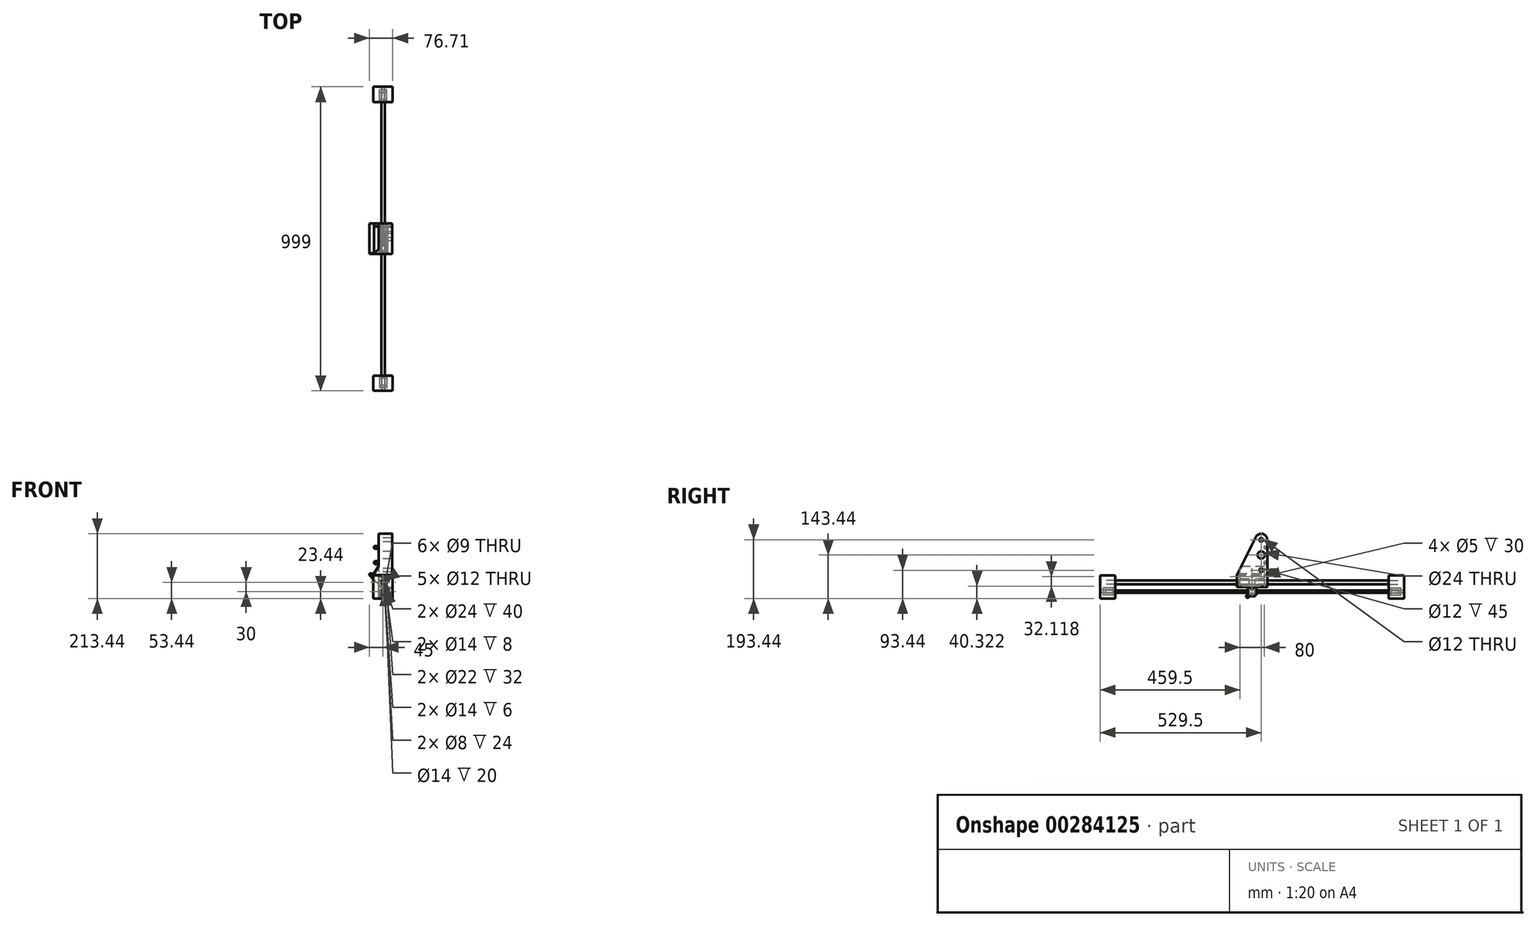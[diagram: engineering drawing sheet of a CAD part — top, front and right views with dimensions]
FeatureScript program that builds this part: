
annotation { "Feature Type Name" : "Feature", "Feature Type Description" : "" }
export const myFeature = defineFeature(function(context is Context, id is Id, definition is map)
    precondition{}
    {
        {
            var Q0;
            Q0=qCreatedBy(makeId("Front.planeOp"),FACE);
            var sketch = newSketch(context, id + "F0", { "sketchPlane" : qUnion([Q0])});
            skLineSegment(sketch, "E0.bottom", {"start": v(-31.71, 38.44) * mm, "end": v(31.71, 38.44) * mm});
            skLineSegment(sketch, "E0.top", {"start": v(-31.71, -38.44) * mm, "end": v(31.71, -38.44) * mm});
            skLineSegment(sketch, "E0.left", {"start": v(-31.71, 38.44) * mm, "end": v(-31.71, -38.44) * mm});
            skLineSegment(sketch, "E0.right", {"start": v(31.71, 38.44) * mm, "end": v(31.71, -38.44) * mm});
            skPoint(sketch, "E0.middle", {"position": v(0, 0) * mm});
            skCircle(sketch, "E1", {"center": v(0, 15) * mm, "radius": 6 * mm});
            skCircle(sketch, "E2", {"center": v(0, -15) * mm, "radius": 12 * mm});
            skCircle(sketch, "E3", {"center": v(0, -15) * mm, "radius": 4.5 * mm});
            skPoint(sketch, "E4", {"position": v(0, 21) * mm});
            skSolve(sketch);
        }
        {
            var Q0;
            Q0=qSketchRegion(id+"F0",true);
            extrude(context, id + "F1", {"entities" : qUnion([Q0]), "oppositeDirection" : true, "depth" : 50 * mm});
        }
        {
            var Q0;
            Q0=makeQuery(id+"F0.imprint","IMPRINT",FACE,{"disambiguationData":[TD([[makeQuery(id+"F0.imprint","IMPRINT",EDGE,{"derivedFrom":sQuery(id+"F0.wireOp",EDGE,"E0.bottom")}),-1.0]])]});
            cPlane(context, id + "F2", {"entities" : qUnion([Q0]), "cplaneType" : CPlaneType.OFFSET, "offset" : 499.5 * mm, "oppositeDirection" : true, "width" : 150 * mm, "height" : 150 * mm});
        }
        {
            var Q0;
            Q0=makeQuery(id+"F0.imprint","IMPRINT",FACE,{"disambiguationData":[TD([[makeQuery(id+"F0.imprint","IMPRINT",EDGE,{"derivedFrom":sQuery(id+"F0.wireOp",EDGE,"E2")}),1.0]])]});
            var Q1;
            Q1=sQuery(id+"F0.wireOp",EDGE,"E2");
            extrude(context, id + "F3", {"entities" : qUnion([Q0]), "operationType" : NewBodyOperationType.ADD, "surfaceEntities" : qUnion([Q1]), "oppositeDirection" : true, "depth" : 10 * mm});
        }
        {
            var Q0;
            Q0=qCreatedBy(makeId("Right.planeOp"),FACE);
            var sketch = newSketch(context, id + "F4", { "sketchPlane" : qUnion([Q0])});
            skPoint(sketch, "E5", {"position": v(0, -15) * mm});
            skLineSegment(sketch, "E6.bottom", {"start": v(0, -15) * mm, "end": v(999, -15) * mm});
            skLineSegment(sketch, "E6.top", {"start": v(0, -11) * mm, "end": v(999, -11) * mm});
            skLineSegment(sketch, "E6.left", {"start": v(0, -15) * mm, "end": v(0, -11) * mm});
            skLineSegment(sketch, "E6.right", {"start": v(999, -15) * mm, "end": v(999, -11) * mm});
            skPoint(sketch, "E7", {"position": v(50, -11) * mm});
            skLineSegment(sketch, "E8.bottom", {"start": v(50, -11) * mm, "end": v(949, -11) * mm});
            skLineSegment(sketch, "E8.top", {"start": v(50, -9) * mm, "end": v(949, -9) * mm});
            skLineSegment(sketch, "E8.left", {"start": v(50, -11) * mm, "end": v(50, -9) * mm});
            skLineSegment(sketch, "E8.right", {"start": v(949, -11) * mm, "end": v(949, -9) * mm});
            skPoint(sketch, "E9", {"position": v(499.5, -15) * mm});
            skLineSegment(sketch, "E10", {"start": v(499.5, -15) * mm, "end": v(499.5, -9) * mm});
            skSolve(sketch);
        }
        {
            var Q0;
            Q0=makeQuery(id+"F4.imprint","IMPRINT",FACE,{"disambiguationData":[TD([[makeQuery(id+"F4.imprint","IMPRINT",EDGE,{"derivedFrom":sQuery(id+"F4.wireOp",EDGE,"E6.bottom")}),1.0]])]});
            var Q1;
            Q1=makeQuery(id+"F4.imprint","IMPRINT",FACE,{"disambiguationData":[TD([[makeQuery(id+"F4.imprint","IMPRINT",EDGE,{"derivedFrom":sQuery(id+"F4.wireOp",EDGE,"E8.bottom")}),1.0]])]});
            var Q2;
            Q2=sQuery(id+"F4.wireOp",EDGE,"E6.bottom");
            revolve(context, id + "F5", {"entities" : qUnion([Q0, Q1]), "axis" : qUnion([Q2]), "revolveType" : RevolveType.FULL});
        }
        {
            var Q0;
            Q0=qCreatedBy(makeId("Right.planeOp"),FACE);
            var sketch = newSketch(context, id + "F6", { "sketchPlane" : qUnion([Q0])});
            skLineSegment(sketch, "E11.bottom", {"start": v(0, 15) * mm, "end": v(999, 15) * mm});
            skLineSegment(sketch, "E11.top", {"start": v(0, 21) * mm, "end": v(999, 21) * mm});
            skLineSegment(sketch, "E11.left", {"start": v(0, 15) * mm, "end": v(0, 21) * mm});
            skLineSegment(sketch, "E11.right", {"start": v(999, 15) * mm, "end": v(999, 21) * mm});
            skPoint(sketch, "E12", {"position": v(499.5, 15) * mm});
            skPoint(sketch, "E13", {"position": v(499.5, 21) * mm});
            skLineSegment(sketch, "E14", {"start": v(499.5, 21) * mm, "end": v(499.5, 15) * mm});
            skSolve(sketch);
        }
        {
            var Q0;
            Q0=qSketchRegion(id+"F6",true);
            var Q1;
            Q1=sQuery(id+"F6.wireOp",EDGE,"E11.bottom");
            revolve(context, id + "F7", {"entities" : qUnion([Q0]), "axis" : qUnion([Q1]), "revolveType" : RevolveType.FULL});
        }
        {
            var Q0;
            Q0=sQuery(id+"F4.wireOp",EDGE,"E10");
            cPoint(context, id + "F8", {"entities" : qUnion([Q0]), "parameter" : 0.5});
        }
        {
            var Q0;
            Q0=sQuery(id+"F4.wireOp",EDGE,"E6.bottom");
            var Q1;
            Q1=qCreatedBy(id+"F8",VERTEX);
            cPlane(context, id + "F9", {"entities" : qUnion([Q0, Q1]), "cplaneType" : CPlaneType.LINE_ANGLE, "offset" : 499.5 * mm, "angle" : 0 * degree, "oppositeDirection" : true, "width" : 150 * mm, "height" : 150 * mm});
        }
        {
            var Q0;
            Q0=makeQuery(id+"F3.opExtrude","CAP_FACE",FACE,{"disambiguationData":[OSD([sQuery(id+"F0.wireOp",EDGE,"E2")])],"isStart":false});
            var sketch = newSketch(context, id + "F10", { "sketchPlane" : qUnion([Q0])});
            skCircle(sketch, "E15", {"center": v(0, -15) * mm, "radius": 12 * mm});
            skCircle(sketch, "E16", {"center": v(0, -15) * mm, "radius": 4 * mm});
            skSolve(sketch);
        }
        {
            var Q0;
            Q0=makeQuery(id+"F10.imprint","IMPRINT",FACE,{"disambiguationData":[TD([[makeQuery(id+"F10.imprint","IMPRINT",EDGE,{"derivedFrom":sQuery(id+"F10.wireOp",EDGE,"E15")}),1.0]])]});
            var Q1;
            Q1=makeQuery(id+"F10.imprint","IMPRINT",FACE,{"disambiguationData":[TD([[makeQuery(id+"F10.imprint","IMPRINT",EDGE,{"derivedFrom":sQuery(id+"F10.wireOp",EDGE,"E15")}),-1.0]])]});
            extrude(context, id + "F11", {"entities" : qUnion([Q0, Q1]), "depth" : 8 * mm});
        }
        {
            var Q0;
            Q0=makeQuery(id+"F11.opExtrude","SWEPT_BODY",BODY,{"disambiguationData":[OSD([sQuery(id+"F10.wireOp",EDGE,"E15"),sQuery(id+"F10.wireOp",EDGE,"E16")])]});
            var Q1;
            Q1=makeQuery(id+"F11.opExtrude","SWEPT_BODY",BODY,{"disambiguationData":[OSD([sQuery(id+"F0.wireOp",EDGE,"E2")])]});
            transform(context, id + "F12", {"entities" : qUnion([Q0, Q1]), "transformType" : TransformType.TRANSLATION_3D, "dx" : 0 * mm, "dy" : 32 * mm, "dz" : 0 * mm, "makeCopy" : true});
        }
        {
            var Q0;
            Q0=makeQuery(id+"F11.opExtrude","CAP_FACE",FACE,{"disambiguationData":[OSD([sQuery(id+"F10.wireOp",EDGE,"E15"),sQuery(id+"F10.wireOp",EDGE,"E16")])],"isStart":false});
            var sketch = newSketch(context, id + "F13", { "sketchPlane" : qUnion([Q0])});
            skCircle(sketch, "E17", {"center": v(0, -15) * mm, "radius": 4 * mm});
            skCircle(sketch, "E18", {"center": v(0, -15) * mm, "radius": 6 * mm});
            skSolve(sketch);
        }
        {
            var Q0;
            Q0=qSketchRegion(id+"F13",true);
            var Q1;
            Q1=makeQuery(id+"F12.opPattern","COPY",FACE,{"derivedFrom":makeQuery(id+"F11.opExtrude","CAP_FACE",FACE,{"disambiguationData":[OSD([sQuery(id+"F10.wireOp",EDGE,"E15"),sQuery(id+"F10.wireOp",EDGE,"E16")])],"isStart":true}),"instanceName":"1"});
            var Q2;
            Q2=makeQuery(id+"F12.opPattern","COPY",BODY,{"derivedFrom":makeQuery(id+"F11.opExtrude","SWEPT_BODY",BODY,{"disambiguationData":[OSD([sQuery(id+"F10.wireOp",EDGE,"E15"),sQuery(id+"F10.wireOp",EDGE,"E16")])]}),"instanceName":"1"});
            extrude(context, id + "F14", {"entities" : qUnion([Q0]), "endBound" : BoundingType.UP_TO_SURFACE, "endBoundEntityFace" : qUnion([Q1]), "endBoundEntityBody" : qUnion([Q2]), "depth" : 33.5 * mm});
        }
        {
            var Q0;
            Q0=makeQuery(id+"F1.opExtrude","SWEPT_BODY",BODY,{"disambiguationData":[OSD([sQuery(id+"F0.wireOp",EDGE,"E0.bottom"),sQuery(id+"F0.wireOp",EDGE,"E0.top"),sQuery(id+"F0.wireOp",EDGE,"E0.left"),sQuery(id+"F0.wireOp",EDGE,"E0.right"),sQuery(id+"F0.wireOp",EDGE,"E1"),sQuery(id+"F0.wireOp",EDGE,"E2")])]});
            var Q1;
            Q1=makeQuery(id+"F11.opExtrude","SWEPT_BODY",BODY,{"disambiguationData":[OSD([sQuery(id+"F0.wireOp",EDGE,"E3"),sQuery(id+"F10.wireOp",EDGE,"E15")])]});
            var Q2;
            Q2=makeQuery(id+"F12.opPattern","COPY",BODY,{"derivedFrom":makeQuery(id+"F11.opExtrude","SWEPT_BODY",BODY,{"disambiguationData":[OSD([sQuery(id+"F0.wireOp",EDGE,"E3"),sQuery(id+"F10.wireOp",EDGE,"E15")])]}),"instanceName":"1"});
            var Q3;
            Q3=makeQuery(id+"F14.opExtrude","SWEPT_BODY",BODY,{"disambiguationData":[OSD([sQuery(id+"F13.wireOp",EDGE,"E17"),sQuery(id+"F13.wireOp",EDGE,"E18")])]});
            var Q4;
            Q4=qCreatedBy(id+"F2.planeOp",FACE);
            mirror(context, id + "F15", {"entities" : qUnion([Q0, Q1, Q2, Q3]), "mirrorPlane" : qUnion([Q4])});
        }
        {
            var Q0;
            Q0=qCreatedBy(id+"F9.planeOp",FACE);
            var sketch = newSketch(context, id + "F16", { "sketchPlane" : qUnion([Q0])});
            skLineSegment(sketch, "E19.bottom", {"start": v(549.5, 29) * mm, "end": v(449.5, 29) * mm});
            skPoint(sketch, "E19.middle", {"position": v(499.5, 15) * mm});
            skPoint(sketch, "E20.middle", {"position": v(499.5, -15) * mm});
            skPoint(sketch, "E21.middle", {"position": v(529.5, 15) * mm});
            skArc(sketch, "E22.MirrorCS", {"start": v(514.5, -26) * mm, "mid": v(510.96, -27.46) * mm, "end": v(509.5, -31) * mm});
            skLineSegment(sketch, "E23", {"start": v(514.5, -26) * mm, "end": v(514.5, 1) * mm});
            skLineSegment(sketch, "E24", {"start": v(509.5, -31) * mm, "end": v(489.5, -31) * mm});
            skLineSegment(sketch, "E25", {"start": v(484.5, -26) * mm, "end": v(484.5, 1) * mm});
            skPoint(sketch, "E26", {"position": v(484.5, -31) * mm});
            skArc(sketch, "E27", {"start": v(484.5, -26) * mm, "mid": v(488.04, -27.46) * mm, "end": v(489.5, -31) * mm});
            skLineSegment(sketch, "E28", {"start": v(549.5, 1) * mm, "end": v(514.5, 1) * mm});
            skLineSegment(sketch, "E29", {"start": v(484.5, 1) * mm, "end": v(449.5, 1) * mm});
            skLineSegment(sketch, "E30", {"start": v(549.5, 1) * mm, "end": v(549.5, 29) * mm});
            skLineSegment(sketch, "E31", {"start": v(449.5, 29) * mm, "end": v(449.5, 1) * mm});
            skSolve(sketch);
        }
        {
            var Q0;
            {var subQ1=sQuery(id+"F16.wireOp",EDGE,"E20.bottom");Q0=makeQuery(id+"F16.imprint","IMPRINT",FACE,{"disambiguationData":[TD([[makeQuery(id+"F16.imprint","IMPRINT",EDGE,{"derivedFrom":subQ1}),1.0]])]});}
            var Q1;
            Q1=makeQuery(id+"F16.imprint","IMPRINT",FACE,{"disambiguationData":[TD([[makeQuery(id+"F16.imprint","IMPRINT",EDGE,{"derivedFrom":sQuery(id+"F16.wireOp",EDGE,"E19.bottom")}),1.0]])]});
            var Q2;
            Q2=makeQuery(id+"F16.imprint","IMPRINT",FACE,{"disambiguationData":[TD([[makeQuery(id+"F16.imprint","IMPRINT",EDGE,{"derivedFrom":sQuery(id+"F16.wireOp",EDGE,"E22.MirrorCS")}),-1.0]])]});
            extrude(context, id + "F17", {"entities" : qUnion([Q0, Q1, Q2]), "depth" : 15 * mm});
        }
        {
            var Q0;
            {var subQ0=sQuery(id+"F16.wireOp",EDGE,"E31");var subQ1=sQuery(id+"F16.wireOp",EDGE,"E30");var subQ2=sQuery(id+"F16.wireOp",EDGE,"E29");var subQ3=sQuery(id+"F16.wireOp",EDGE,"E28");var subQ4=sQuery(id+"F16.wireOp",EDGE,"E27");var subQ5=sQuery(id+"F16.wireOp",EDGE,"E25");var subQ6=sQuery(id+"F16.wireOp",EDGE,"E24");var subQ7=sQuery(id+"F16.wireOp",EDGE,"E23");var subQ8=sQuery(id+"F16.wireOp",EDGE,"E22.MirrorCS");var subQ9=sQuery(id+"F16.wireOp",EDGE,"E19.bottom");Q0=makeQuery(id+"F32.boolean.opBoolean","MERGE",FACE,{"derivedFrom":[makeQuery(id+"F17.opExtrude","CAP_FACE",FACE,{"disambiguationData":[OSD([subQ9,subQ8,subQ7,subQ6,subQ5,subQ4,subQ3,subQ2,subQ1,subQ0])],"isStart":false}),makeQuery(id+"F32.opExtrude","CAP_FACE",FACE,{"disambiguationData":[OSD([subQ9,subQ8,subQ7,subQ6,subQ5,subQ4,subQ3,subQ2,subQ1,subQ0]),ownerDisambiguation([makeQuery(id+"F32.opExtrude","SWEPT_BODY",BODY,{"disambiguationData":[OSD([sQuery(id+"F31.wireOp",EDGE,"E61"),sQuery(id+"F31.wireOp",EDGE,"E62")])]})])],"isStart":false}),makeQuery(id+"F32.opExtrude","CAP_FACE",FACE,{"disambiguationData":[OSD([subQ9,subQ8,subQ7,subQ6,subQ5,subQ4,subQ3,subQ2,subQ1,subQ0]),ownerDisambiguation([makeQuery(id+"F32.opExtrude","SWEPT_BODY",BODY,{"disambiguationData":[OSD([sQuery(id+"F31.wireOp",EDGE,"E63.MirrorC"),sQuery(id+"F31.wireOp",EDGE,"E64.MirrorC")])]})])],"isStart":false})]});}
            var sketch = newSketch(context, id + "F18", { "sketchPlane" : qUnion([Q0])});
            skLineSegment(sketch, "E32.bottom", {"start": v(449.5, 29) * mm, "end": v(549.5, 29) * mm});
            skLineSegment(sketch, "E32.top", {"start": v(449.5, 39) * mm, "end": v(549.5, 39) * mm});
            skLineSegment(sketch, "E32.left", {"start": v(449.5, 29) * mm, "end": v(449.5, 39) * mm});
            skLineSegment(sketch, "E32.right", {"start": v(549.5, 29) * mm, "end": v(549.5, 39) * mm});
            skCircle(sketch, "E33", {"center": v(459.5, 34) * mm, "radius": 2.5 * mm});
            skCircle(sketch, "E34.MirrorC", {"center": v(539.5, 34) * mm, "radius": 2.5 * mm});
            skLineSegment(sketch, "E35", {"start": v(539.5, 34) * mm, "end": v(459.5, 34) * mm});
            skPoint(sketch, "E36", {"position": v(499.5, 34) * mm});
            skCircle(sketch, "E37", {"center": v(499.5, 34) * mm, "radius": 2.5 * mm});
            skSolve(sketch);
        }
        {
            var Q0;
            Q0=makeQuery(id+"F18.imprint","IMPRINT",FACE,{"disambiguationData":[TD([[makeQuery(id+"F18.imprint","IMPRINT",EDGE,{"derivedFrom":sQuery(id+"F18.wireOp",EDGE,"E32.bottom")}),-1.0]])]});
            extrude(context, id + "F19", {"entities" : qUnion([Q0]), "operationType" : NewBodyOperationType.ADD, "oppositeDirection" : true, "depth" : 10 * mm});
        }
        {
            var Q0;
            Q0=makeQuery(id+"F17.opExtrude","CAP_FACE",FACE,{"disambiguationData":[OSD([sQuery(id+"F16.wireOp",EDGE,"E19.bottom"),sQuery(id+"F16.wireOp",EDGE,"E19.top"),sQuery(id+"F16.wireOp",EDGE,"E19.left"),sQuery(id+"F16.wireOp",EDGE,"E19.right"),sQuery(id+"F16.wireOp",EDGE,"E20.top"),sQuery(id+"F16.wireOp",EDGE,"E20.left"),sQuery(id+"F16.wireOp",EDGE,"E20.right")])],"isStart":true});
            var sketch = newSketch(context, id + "F20", { "sketchPlane" : qUnion([Q0])});
            skLineSegment(sketch, "E38.bottom", {"start": v(-489.5, 15) * mm, "end": v(-457.5, 15) * mm});
            skLineSegment(sketch, "E39.MirrorCS", {"start": v(-509.5, 15) * mm, "end": v(-541.5, 15) * mm});
            skLineSegment(sketch, "E40.bottom", {"start": v(-549.5, 15) * mm, "end": v(-541.5, 15) * mm});
            skLineSegment(sketch, "E41.top", {"start": v(-509.5, 15) * mm, "end": v(-489.5, 15) * mm});
            skLineSegment(sketch, "E42.top", {"start": v(-457.5, 15) * mm, "end": v(-449.5, 15) * mm});
            skLineSegment(sketch, "E43.left", {"start": v(-549.5, 15) * mm, "end": v(-549.5, 22) * mm});
            skLineSegment(sketch, "E43.right", {"start": v(-449.5, 15) * mm, "end": v(-449.5, 22) * mm});
            skLineSegment(sketch, "E44", {"start": v(-549.5, 22) * mm, "end": v(-541.5, 22) * mm});
            skLineSegment(sketch, "E45", {"start": v(-541.5, 26) * mm, "end": v(-541.5, 22) * mm});
            skLineSegment(sketch, "E46", {"start": v(-541.5, 26) * mm, "end": v(-509.5, 26) * mm});
            skLineSegment(sketch, "E47", {"start": v(-509.5, 26) * mm, "end": v(-509.5, 22) * mm});
            skLineSegment(sketch, "E48", {"start": v(-509.5, 22) * mm, "end": v(-489.5, 22) * mm});
            skLineSegment(sketch, "E49", {"start": v(-489.5, 22) * mm, "end": v(-489.5, 26) * mm});
            skLineSegment(sketch, "E50", {"start": v(-489.5, 26) * mm, "end": v(-457.5, 26) * mm});
            skLineSegment(sketch, "E51", {"start": v(-457.5, 26) * mm, "end": v(-457.5, 22) * mm});
            skLineSegment(sketch, "E52", {"start": v(-457.5, 22) * mm, "end": v(-449.5, 22) * mm});
            skSolve(sketch);
        }
        {
            var Q0;
            Q0=qSketchRegion(id+"F20",true);
            var Q1;
            Q1=sQuery(id+"F6.wireOp",EDGE,"E11.bottom");
            revolve(context, id + "F21", {"operationType" : NewBodyOperationType.REMOVE, "entities" : qUnion([Q0]), "axis" : qUnion([Q1]), "revolveType" : RevolveType.ONE_DIRECTION, "angle" : 180 * degree});
        }
        {
            var Q0;
            Q0=qCreatedBy(id+"F9.planeOp",FACE);
            var sketch = newSketch(context, id + "F22", { "sketchPlane" : qUnion([Q0])});
            skLineSegment(sketch, "E53.bottom", {"start": v(489.5, 21) * mm, "end": v(457.5, 21) * mm});
            skLineSegment(sketch, "E53.top", {"start": v(489.5, 26) * mm, "end": v(457.5, 26) * mm});
            skLineSegment(sketch, "E53.left", {"start": v(489.5, 21) * mm, "end": v(489.5, 26) * mm});
            skLineSegment(sketch, "E53.right", {"start": v(457.5, 21) * mm, "end": v(457.5, 26) * mm});
            skSolve(sketch);
        }
        {
            var Q0;
            Q0=makeQuery(id+"F22.imprint","IMPRINT",FACE,{"disambiguationData":[TD([[makeQuery(id+"F22.imprint","IMPRINT",EDGE,{"derivedFrom":sQuery(id+"F22.wireOp",EDGE,"E53.bottom")}),-1.0]])]});
            var Q1;
            Q1=sQuery(id+"F6.wireOp",EDGE,"E11.bottom");
            revolve(context, id + "F23", {"entities" : qUnion([Q0]), "axis" : qUnion([Q1]), "revolveType" : RevolveType.FULL});
        }
        {
            var Q0;
            Q0=makeQuery(id+"F23.opRevolve","SWEPT_BODY",BODY,{"disambiguationData":[OSD([sQuery(id+"F22.wireOp",EDGE,"E53.bottom"),sQuery(id+"F22.wireOp",EDGE,"E53.top"),sQuery(id+"F22.wireOp",EDGE,"E53.left"),sQuery(id+"F22.wireOp",EDGE,"E53.right")])]});
            var Q1;
            Q1=qCreatedBy(id+"F2.planeOp",FACE);
            mirror(context, id + "F24", {"entities" : qUnion([Q0]), "mirrorPlane" : qUnion([Q1])});
        }
        {
            var Q0;
            Q0=qCreatedBy(id+"F2.planeOp",FACE);
            var sketch = newSketch(context, id + "F25", { "sketchPlane" : qUnion([Q0])});
            skCircle(sketch, "E54.cCircle", {"center": v(0, -15) * mm, "radius": 9.5 * mm, "construction": true});
            skLineSegment(sketch, "E54.0", {"start": v(0.1, -4.03) * mm, "end": v(9.55, -9.6) * mm});
            skLineSegment(sketch, "E54.1", {"start": v(9.55, -9.6) * mm, "end": v(9.45, -20.57) * mm});
            skLineSegment(sketch, "E54.2", {"start": v(9.45, -20.57) * mm, "end": v(-0.1, -25.97) * mm});
            skLineSegment(sketch, "E54.3", {"start": v(-0.1, -25.97) * mm, "end": v(-9.55, -20.4) * mm});
            skLineSegment(sketch, "E54.4", {"start": v(-9.55, -20.4) * mm, "end": v(-9.45, -9.43) * mm});
            skLineSegment(sketch, "E54.5", {"start": v(-9.45, -9.43) * mm, "end": v(0.1, -4.03) * mm});
            skPoint(sketch, "E54.0.midPoint", {"position": v(4.83, -6.82) * mm});
            skSolve(sketch);
        }
        {
            var Q0;
            Q0=qSketchRegion(id+"F25",true);
            extrude(context, id + "F26", {"entities" : qUnion([Q0]), "operationType" : NewBodyOperationType.REMOVE, "endBound" : BoundingType.SYMMETRIC, "depth" : 18 * mm});
        }
        {
            var Q0;
            Q0=makeQuery(id+"F16.imprint","IMPRINT",FACE,{"disambiguationData":[TD([[makeQuery(id+"F16.imprint","IMPRINT",EDGE,{"derivedFrom":sQuery(id+"F16.wireOp",EDGE,"E19.bottom")}),1.0]])]});
            var sketch = newSketch(context, id + "F27", { "sketchPlane" : qUnion([Q0])});
            skLineSegment(sketch, "E55.bottom", {"start": v(514.5, -15) * mm, "end": v(484.5, -15) * mm});
            skLineSegment(sketch, "E55.top", {"start": v(514.5, -8) * mm, "end": v(484.5, -8) * mm});
            skLineSegment(sketch, "E55.left", {"start": v(514.5, -15) * mm, "end": v(514.5, -8) * mm});
            skLineSegment(sketch, "E55.right", {"start": v(484.5, -15) * mm, "end": v(484.5, -8) * mm});
            skSolve(sketch);
        }
        {
            var Q0;
            Q0=qSketchRegion(id+"F27",true);
            var Q1;
            Q1=sQuery(id+"F4.wireOp",EDGE,"E6.bottom");
            revolve(context, id + "F28", {"operationType" : NewBodyOperationType.REMOVE, "entities" : qUnion([Q0]), "axis" : qUnion([Q1]), "revolveType" : RevolveType.FULL});
        }
        {
            var Q0;
            Q0=qCreatedBy(id+"F2.planeOp",FACE);
            var sketch = newSketch(context, id + "F29", { "sketchPlane" : qUnion([Q0])});
            skCircle(sketch, "E56.cCircle", {"center": v(0, -15) * mm, "radius": 9.5 * mm, "construction": true});
            skLineSegment(sketch, "E56.0", {"start": v(-9.5, -9.51) * mm, "end": v(0, -4.03) * mm});
            skLineSegment(sketch, "E56.1", {"start": v(0, -4.03) * mm, "end": v(9.5, -9.52) * mm});
            skLineSegment(sketch, "E56.2", {"start": v(9.5, -9.52) * mm, "end": v(9.5, -20.49) * mm});
            skLineSegment(sketch, "E56.3", {"start": v(9.5, -20.49) * mm, "end": v(0, -25.97) * mm});
            skLineSegment(sketch, "E56.4", {"start": v(0, -25.97) * mm, "end": v(-9.5, -20.48) * mm});
            skLineSegment(sketch, "E56.5", {"start": v(-9.5, -20.48) * mm, "end": v(-9.5, -9.51) * mm});
            skPoint(sketch, "E56.0.midPoint", {"position": v(-4.75, -6.77) * mm});
            skCircle(sketch, "E57", {"center": v(0, -15) * mm, "radius": 6 * mm});
            skSolve(sketch);
        }
        {
            var Q0;
            Q0=qSketchRegion(id+"F29",true);
            extrude(context, id + "F30", {"entities" : qUnion([Q0]), "endBound" : BoundingType.SYMMETRIC, "depth" : 18 * mm});
        }
        {
            var Q0;
            Q0=qCreatedBy(id+"F9.planeOp",FACE);
            var sketch = newSketch(context, id + "F31", { "sketchPlane" : qUnion([Q0])});
            skLineSegment(sketch, "E58", {"start": v(499.5, 8) * mm, "end": v(499.5, -4.09) * mm});
            skPoint(sketch, "E59", {"position": v(499.5, 1.96) * mm});
            skPoint(sketch, "E60", {"position": v(484.5, -31) * mm});
            skCircle(sketch, "E61", {"center": v(484.5, -31) * mm, "radius": 2.5 * mm});
            skCircle(sketch, "E62", {"center": v(484.5, -31) * mm, "radius": 5 * mm});
            skCircle(sketch, "E63.MirrorC", {"center": v(514.5, -31) * mm, "radius": 5 * mm});
            skCircle(sketch, "E64.MirrorC", {"center": v(514.5, -31) * mm, "radius": 2.5 * mm});
            skSolve(sketch);
        }
        {
            var Q0;
            Q0=makeQuery(id+"F31.imprint","IMPRINT",FACE,{"disambiguationData":[TD([[makeQuery(id+"F31.imprint","IMPRINT",EDGE,{"derivedFrom":sQuery(id+"F31.wireOp",EDGE,"E61")}),-1.0]])]});
            var Q1;
            Q1=makeQuery(id+"F31.imprint","IMPRINT",FACE,{"disambiguationData":[TD([[makeQuery(id+"F31.imprint","IMPRINT",EDGE,{"derivedFrom":sQuery(id+"F31.wireOp",EDGE,"E63.MirrorC")}),-1.0]])]});
            var Q2;
            Q2=makeQuery(id+"F17.opExtrude","CAP_FACE",FACE,{"disambiguationData":[OSD([sQuery(id+"F16.wireOp",EDGE,"E19.bottom"),sQuery(id+"F16.wireOp",EDGE,"E19.top"),sQuery(id+"F16.wireOp",EDGE,"E19.left"),sQuery(id+"F16.wireOp",EDGE,"E19.right"),sQuery(id+"F16.wireOp",EDGE,"E20.top"),sQuery(id+"F16.wireOp",EDGE,"E20.left"),sQuery(id+"F16.wireOp",EDGE,"E20.right")])],"isStart":false});
            extrude(context, id + "F32", {"entities" : qUnion([Q0, Q1]), "operationType" : NewBodyOperationType.ADD, "endBound" : BoundingType.UP_TO_SURFACE, "endBoundEntityFace" : qUnion([Q2]), "depth" : 25 * mm});
        }
        {
            var Q0;
            {var subQ3=sQuery(id+"F27.wireOp",EDGE,"E55.top");Q0=makeQuery(id+"F27.imprint","IMPRINT",FACE,{"disambiguationData":[TD([[makeQuery(id+"F27.imprint","IMPRINT",EDGE,{"derivedFrom":subQ3}),-1.0]])]});}
            var sketch = newSketch(context, id + "F33", { "sketchPlane" : qUnion([Q0])});
            skCircle(sketch, "E65", {"center": v(499.49, 1.88) * mm, "radius": 2.5 * mm});
            skSolve(sketch);
        }
        {
            var Q0;
            Q0=qSketchRegion(id+"F33",true);
            var Q1;
            {var subQ0=sQuery(id+"F16.wireOp",EDGE,"E31");var subQ1=sQuery(id+"F16.wireOp",EDGE,"E30");var subQ2=sQuery(id+"F16.wireOp",EDGE,"E29");var subQ3=sQuery(id+"F16.wireOp",EDGE,"E28");var subQ4=sQuery(id+"F16.wireOp",EDGE,"E27");var subQ5=sQuery(id+"F16.wireOp",EDGE,"E25");var subQ6=sQuery(id+"F16.wireOp",EDGE,"E24");var subQ7=sQuery(id+"F16.wireOp",EDGE,"E23");var subQ8=sQuery(id+"F16.wireOp",EDGE,"E22.MirrorCS");var subQ9=sQuery(id+"F16.wireOp",EDGE,"E19.bottom");Q1=makeQuery(id+"F32.boolean.opBoolean","MERGE",FACE,{"derivedFrom":[makeQuery(id+"F17.opExtrude","CAP_FACE",FACE,{"disambiguationData":[OSD([subQ9,subQ8,subQ7,subQ6,subQ5,subQ4,subQ3,subQ2,subQ1,subQ0])],"isStart":false}),makeQuery(id+"F32.opExtrude","CAP_FACE",FACE,{"disambiguationData":[OSD([subQ9,subQ8,subQ7,subQ6,subQ5,subQ4,subQ3,subQ2,subQ1,subQ0]),ownerDisambiguation([makeQuery(id+"F32.opExtrude","SWEPT_BODY",BODY,{"disambiguationData":[OSD([sQuery(id+"F31.wireOp",EDGE,"E61"),sQuery(id+"F31.wireOp",EDGE,"E62")])]})])],"isStart":false}),makeQuery(id+"F32.opExtrude","CAP_FACE",FACE,{"disambiguationData":[OSD([subQ9,subQ8,subQ7,subQ6,subQ5,subQ4,subQ3,subQ2,subQ1,subQ0]),ownerDisambiguation([makeQuery(id+"F32.opExtrude","SWEPT_BODY",BODY,{"disambiguationData":[OSD([sQuery(id+"F31.wireOp",EDGE,"E63.MirrorC"),sQuery(id+"F31.wireOp",EDGE,"E64.MirrorC")])]})])],"isStart":false})]});}
            extrude(context, id + "F34", {"entities" : qUnion([Q0]), "operationType" : NewBodyOperationType.REMOVE, "endBound" : BoundingType.UP_TO_SURFACE, "endBoundEntityFace" : qUnion([Q1]), "depth" : 25 * mm});
        }
        {
            var Q0;
            Q0=makeQuery(id+"F17.opExtrude","SWEPT_BODY",BODY,{"disambiguationData":[OSD([sQuery(id+"F16.wireOp",EDGE,"E19.bottom"),sQuery(id+"F16.wireOp",EDGE,"E22.MirrorCS"),sQuery(id+"F16.wireOp",EDGE,"E23"),sQuery(id+"F16.wireOp",EDGE,"E24"),sQuery(id+"F16.wireOp",EDGE,"E25"),sQuery(id+"F16.wireOp",EDGE,"E27"),sQuery(id+"F16.wireOp",EDGE,"E28"),sQuery(id+"F16.wireOp",EDGE,"E29"),sQuery(id+"F16.wireOp",EDGE,"E30"),sQuery(id+"F16.wireOp",EDGE,"E31")])]});
            var Q1;
            Q1=qCreatedBy(id+"F9.planeOp",FACE);
            mirror(context, id + "F35", {"entities" : qUnion([Q0]), "mirrorPlane" : qUnion([Q1])});
        }
        {
            var Q0;
            Q0=makeQuery(id+"F19.opExtrude","CAP_FACE",FACE,{"disambiguationData":[OSD([sQuery(id+"F18.wireOp",EDGE,"E32.bottom"),sQuery(id+"F18.wireOp",EDGE,"E32.top"),sQuery(id+"F18.wireOp",EDGE,"E32.left"),sQuery(id+"F18.wireOp",EDGE,"E32.right"),sQuery(id+"F18.wireOp",EDGE,"E33"),sQuery(id+"F18.wireOp",EDGE,"E34.MirrorC")])],"isStart":false});
            var Q1;
            Q1=makeQuery(id+"F35.opPattern","COPY",FACE,{"derivedFrom":makeQuery(id+"F19.opExtrude","CAP_FACE",FACE,{"disambiguationData":[OSD([sQuery(id+"F18.wireOp",EDGE,"E32.bottom"),sQuery(id+"F18.wireOp",EDGE,"E32.top"),sQuery(id+"F18.wireOp",EDGE,"E32.left"),sQuery(id+"F18.wireOp",EDGE,"E32.right"),sQuery(id+"F18.wireOp",EDGE,"E33"),sQuery(id+"F18.wireOp",EDGE,"E34.MirrorC")])],"isStart":false}),"instanceName":"1"});
            var Q2;
            Q2=makeQuery(id+"F35.opPattern","COPY",BODY,{"derivedFrom":makeQuery(id+"F17.opExtrude","SWEPT_BODY",BODY,{"disambiguationData":[OSD([sQuery(id+"F16.wireOp",EDGE,"E19.bottom"),sQuery(id+"F16.wireOp",EDGE,"E22.MirrorCS"),sQuery(id+"F16.wireOp",EDGE,"E23"),sQuery(id+"F16.wireOp",EDGE,"E24"),sQuery(id+"F16.wireOp",EDGE,"E25"),sQuery(id+"F16.wireOp",EDGE,"E27"),sQuery(id+"F16.wireOp",EDGE,"E28"),sQuery(id+"F16.wireOp",EDGE,"E29"),sQuery(id+"F16.wireOp",EDGE,"E30"),sQuery(id+"F16.wireOp",EDGE,"E31")])]}),"instanceName":"1"});
            extrude(context, id + "F36", {"entities" : qUnion([Q0]), "operationType" : NewBodyOperationType.ADD, "endBound" : BoundingType.UP_TO_SURFACE, "endBoundEntityFace" : qUnion([Q1]), "endBoundEntityBody" : qUnion([Q2]), "depth" : 25 * mm});
        }
        {
            var Q0;
            Q0=qCreatedBy(id+"F9.planeOp",FACE);
            var sketch = newSketch(context, id + "F37", { "sketchPlane" : qUnion([Q0])});
            skLineSegment(sketch, "E66", {"start": v(549.5, 39) * mm, "end": v(449.5, 39) * mm});
            skArc(sketch, "E67", {"start": v(549.5, 155) * mm, "mid": v(534.07, 174.47) * mm, "end": v(511.6, 163.9) * mm});
            skCircle(sketch, "E68", {"center": v(529.5, 155) * mm, "radius": 6 * mm});
            skCircle(sketch, "E69", {"center": v(529.5, 55) * mm, "radius": 6 * mm});
            skLineSegment(sketch, "E70", {"start": v(549.5, 39) * mm, "end": v(549.5, 155) * mm});
            skLineSegment(sketch, "E71", {"start": v(449.5, 39) * mm, "end": v(511.6, 163.9) * mm});
            skLineSegment(sketch, "E72", {"start": v(529.5, 155) * mm, "end": v(529.5, 55) * mm});
            skPoint(sketch, "E73", {"position": v(529.5, 105) * mm});
            skCircle(sketch, "E74", {"center": v(529.5, 105) * mm, "radius": 12 * mm});
            skLineSegment(sketch, "E75", {"start": v(549.5, 49) * mm, "end": v(529.5, 49) * mm});
            skPoint(sketch, "E76", {"position": v(549.5, 49) * mm});
            skLineSegment(sketch, "E77", {"start": v(529.5, 105) * mm, "end": v(549.5, 105) * mm});
            skPoint(sketch, "E78", {"position": v(549.5, 105) * mm});
            skSolve(sketch);
        }
        {
            var Q0;
            Q0 = qSketchRegion(id + "F37", true);
            var Q1;
            {var subQ0=sQuery(id+"F18.wireOp",EDGE,"E34.MirrorC");var subQ1=sQuery(id+"F18.wireOp",EDGE,"E33");var subQ2=sQuery(id+"F18.wireOp",EDGE,"E32.right");var subQ3=sQuery(id+"F18.wireOp",EDGE,"E32.left");var subQ4=sQuery(id+"F18.wireOp",EDGE,"E32.top");var subQ5=sQuery(id+"F18.wireOp",EDGE,"E32.bottom");var subQ6=sQuery(id+"F16.wireOp",EDGE,"E31");var subQ7=sQuery(id+"F16.wireOp",EDGE,"E30");var subQ8=sQuery(id+"F16.wireOp",EDGE,"E29");var subQ9=sQuery(id+"F16.wireOp",EDGE,"E28");var subQ10=sQuery(id+"F16.wireOp",EDGE,"E27");var subQ11=sQuery(id+"F16.wireOp",EDGE,"E25");var subQ12=sQuery(id+"F16.wireOp",EDGE,"E24");var subQ13=sQuery(id+"F16.wireOp",EDGE,"E23");var subQ14=sQuery(id+"F16.wireOp",EDGE,"E22.MirrorCS");var subQ15=sQuery(id+"F16.wireOp",EDGE,"E19.bottom");Q1=makeQuery(id+"F32.boolean.opBoolean","MERGE",FACE,{"derivedFrom":[makeQuery(id+"F19.boolean.opBoolean","MERGE",FACE,{"derivedFrom":[makeQuery(id+"F17.opExtrude","CAP_FACE",FACE,{"disambiguationData":[OSD([subQ15,subQ14,subQ13,subQ12,subQ11,subQ10,subQ9,subQ8,subQ7,subQ6])],"isStart":false}),makeQuery(id+"F19.opExtrude","CAP_FACE",FACE,{"disambiguationData":[OSD([subQ5,subQ4,subQ3,subQ2,subQ1,subQ0])],"isStart":true})]}),makeQuery(id+"F32.opExtrude","CAP_FACE",FACE,{"disambiguationData":[OSD([subQ15,subQ14,subQ13,subQ12,subQ11,subQ10,subQ9,subQ8,subQ7,subQ6,subQ5,subQ4,subQ3,subQ2,subQ1,subQ0]),ownerDisambiguation([makeQuery(id+"F32.opExtrude","SWEPT_BODY",BODY,{"disambiguationData":[OSD([sQuery(id+"F31.wireOp",EDGE,"E61"),sQuery(id+"F31.wireOp",EDGE,"E62")])]})])],"isStart":false}),makeQuery(id+"F32.opExtrude","CAP_FACE",FACE,{"disambiguationData":[OSD([subQ15,subQ14,subQ13,subQ12,subQ11,subQ10,subQ9,subQ8,subQ7,subQ6,subQ5,subQ4,subQ3,subQ2,subQ1,subQ0]),ownerDisambiguation([makeQuery(id+"F32.opExtrude","SWEPT_BODY",BODY,{"disambiguationData":[OSD([sQuery(id+"F31.wireOp",EDGE,"E63.MirrorC"),sQuery(id+"F31.wireOp",EDGE,"E64.MirrorC")])]})])],"isStart":false})]});}
            var Q2;
            {var subQ0=sQuery(id+"F18.wireOp",EDGE,"E34.MirrorC");var subQ1=sQuery(id+"F18.wireOp",EDGE,"E33");var subQ2=sQuery(id+"F18.wireOp",EDGE,"E32.right");var subQ3=sQuery(id+"F18.wireOp",EDGE,"E32.left");var subQ4=sQuery(id+"F18.wireOp",EDGE,"E32.top");var subQ5=sQuery(id+"F18.wireOp",EDGE,"E32.bottom");var subQ6=sQuery(id+"F16.wireOp",EDGE,"E31");var subQ7=sQuery(id+"F16.wireOp",EDGE,"E30");var subQ8=sQuery(id+"F16.wireOp",EDGE,"E29");var subQ9=sQuery(id+"F16.wireOp",EDGE,"E28");var subQ10=sQuery(id+"F16.wireOp",EDGE,"E27");var subQ11=sQuery(id+"F16.wireOp",EDGE,"E25");var subQ12=sQuery(id+"F16.wireOp",EDGE,"E24");var subQ13=sQuery(id+"F16.wireOp",EDGE,"E23");var subQ14=sQuery(id+"F16.wireOp",EDGE,"E22.MirrorCS");var subQ15=sQuery(id+"F16.wireOp",EDGE,"E19.bottom");Q2=makeQuery(id+"F35.opPattern","COPY",FACE,{"derivedFrom":makeQuery(id+"F32.boolean.opBoolean","MERGE",FACE,{"derivedFrom":[makeQuery(id+"F19.boolean.opBoolean","MERGE",FACE,{"derivedFrom":[makeQuery(id+"F17.opExtrude","CAP_FACE",FACE,{"disambiguationData":[OSD([subQ15,subQ14,subQ13,subQ12,subQ11,subQ10,subQ9,subQ8,subQ7,subQ6])],"isStart":false}),makeQuery(id+"F19.opExtrude","CAP_FACE",FACE,{"disambiguationData":[OSD([subQ5,subQ4,subQ3,subQ2,subQ1,subQ0])],"isStart":true})]}),makeQuery(id+"F32.opExtrude","CAP_FACE",FACE,{"disambiguationData":[OSD([subQ15,subQ14,subQ13,subQ12,subQ11,subQ10,subQ9,subQ8,subQ7,subQ6,subQ5,subQ4,subQ3,subQ2,subQ1,subQ0]),ownerDisambiguation([makeQuery(id+"F32.opExtrude","SWEPT_BODY",BODY,{"disambiguationData":[OSD([sQuery(id+"F31.wireOp",EDGE,"E61"),sQuery(id+"F31.wireOp",EDGE,"E62")])]})])],"isStart":false}),makeQuery(id+"F32.opExtrude","CAP_FACE",FACE,{"disambiguationData":[OSD([subQ15,subQ14,subQ13,subQ12,subQ11,subQ10,subQ9,subQ8,subQ7,subQ6,subQ5,subQ4,subQ3,subQ2,subQ1,subQ0]),ownerDisambiguation([makeQuery(id+"F32.opExtrude","SWEPT_BODY",BODY,{"disambiguationData":[OSD([sQuery(id+"F31.wireOp",EDGE,"E63.MirrorC"),sQuery(id+"F31.wireOp",EDGE,"E64.MirrorC")])]})])],"isStart":false})]}),"instanceName":"1"});}
            extrude(context, id + "F38", {"entities" : qUnion([Q0]), "endBoundEntityFace" : qUnion([Q1]), "depth" : 30 * mm, "hasSecondDirection" : true, "secondDirectionBound" : SecondDirectionBoundingType.UP_TO_SURFACE, "secondDirectionOppositeDirection" : true, "secondDirectionBoundEntityFace" : qUnion([Q2]), "secondDirectionDepth" : 25 * mm});
        }
        {
            var Q0;
            Q0=qCreatedBy(id+"F2.planeOp",FACE);
            var sketch = newSketch(context, id + "F39", { "sketchPlane" : qUnion([Q0])});
            skPoint(sketch, "E79", {"position": v(-15, 39) * mm});
            skLineSegment(sketch, "E80", {"start": v(-15, 39) * mm, "end": v(-15, 69) * mm});
            skLineSegment(sketch, "E81", {"start": v(-15, 39) * mm, "end": v(-45, 39) * mm});
            skLineSegment(sketch, "E82", {"start": v(-45, 39) * mm, "end": v(-45, 44) * mm});
            skLineSegment(sketch, "E83", {"start": v(-45, 44) * mm, "end": v(-30, 44) * mm});
            skLineSegment(sketch, "E84", {"start": v(-30, 44) * mm, "end": v(-15, 69) * mm});
            skPoint(sketch, "E85", {"position": v(-35, 39) * mm});
            skSolve(sketch);
        }
        {
            var Q0;
            Q0 = qSketchRegion(id + "F39", true);
            var Q1;
            Q1=makeQuery(id+"F38.opExtrude","SWEPT_FACE",FACE,{"disambiguationData":[OSD([sQuery(id+"F37.wireOp",EDGE,"E71")])]});
            var Q2;
            {var subQ0=sQuery(id+"F18.wireOp",EDGE,"E32.right");Q2=makeQuery(id+"F38.boolean.opBoolean","MERGE",FACE,{"derivedFrom":[makeQuery(id+"F36.boolean.opBoolean","MERGE",FACE,{"derivedFrom":[makeQuery(id+"F19.boolean.opBoolean","MERGE",FACE,{"derivedFrom":[makeQuery(id+"F17.opExtrude","SWEPT_FACE",FACE,{"disambiguationData":[OSD([sQuery(id+"F16.wireOp",EDGE,"E30")])]}),makeQuery(id+"F19.opExtrude","SWEPT_FACE",FACE,{"disambiguationData":[OSD([subQ0])]})]}),makeQuery(id+"F36.opExtrude","SWEPT_FACE",FACE,{"disambiguationData":[OSD([subQ0])]})]}),makeQuery(id+"F38.opExtrude","SWEPT_FACE",FACE,{"disambiguationData":[OSD([sQuery(id+"F37.wireOp",EDGE,"E70")])]})]});}
            extrude(context, id + "F40", {"entities" : qUnion([Q0]), "operationType" : NewBodyOperationType.ADD, "endBound" : BoundingType.UP_TO_SURFACE, "endBoundEntityFace" : qUnion([Q1]), "depth" : 25 * mm, "hasSecondDirection" : true, "secondDirectionBound" : SecondDirectionBoundingType.UP_TO_SURFACE, "secondDirectionOppositeDirection" : true, "secondDirectionBoundEntityFace" : qUnion([Q2]), "secondDirectionDepth" : 25 * mm});
        }
        {
            var Q0;
            Q0=qCreatedBy(id+"F2.planeOp",FACE);
            var sketch = newSketch(context, id + "F41", { "sketchPlane" : qUnion([Q0])});
            skLineSegment(sketch, "E86", {"start": v(-15, 9) * mm, "end": v(-45, 39) * mm});
            skLineSegment(sketch, "E87", {"start": v(-45, 39) * mm, "end": v(-15, 39) * mm});
            skLineSegment(sketch, "E88", {"start": v(-15, 39) * mm, "end": v(-15, 9) * mm});
            skSolve(sketch);
        }
        {
            var Q0;
            Q0 = qSketchRegion(id + "F41", true);
            var Q1;
            Q1=makeQuery(id+"F35.opPattern","COPY",FACE,{"derivedFrom":makeQuery(id+"F19.boolean.opBoolean","MERGE",FACE,{"derivedFrom":[makeQuery(id+"F17.opExtrude","SWEPT_FACE",FACE,{"disambiguationData":[OSD([sQuery(id+"F16.wireOp",EDGE,"E31")])]}),makeQuery(id+"F19.opExtrude","SWEPT_FACE",FACE,{"disambiguationData":[OSD([sQuery(id+"F18.wireOp",EDGE,"E32.left")])]})]}),"instanceName":"1"});
            var Q2;
            Q2=makeQuery(id+"F35.opPattern","COPY",FACE,{"derivedFrom":makeQuery(id+"F19.boolean.opBoolean","MERGE",FACE,{"derivedFrom":[makeQuery(id+"F17.opExtrude","SWEPT_FACE",FACE,{"disambiguationData":[OSD([sQuery(id+"F16.wireOp",EDGE,"E30")])]}),makeQuery(id+"F19.opExtrude","SWEPT_FACE",FACE,{"disambiguationData":[OSD([sQuery(id+"F18.wireOp",EDGE,"E32.right")])]})]}),"instanceName":"1"});
            extrude(context, id + "F42", {"entities" : qUnion([Q0]), "endBound" : BoundingType.UP_TO_SURFACE, "endBoundEntityFace" : qUnion([Q1]), "depth" : 25 * mm, "hasSecondDirection" : true, "secondDirectionBound" : SecondDirectionBoundingType.UP_TO_SURFACE, "secondDirectionOppositeDirection" : true, "secondDirectionBoundEntityFace" : qUnion([Q2]), "secondDirectionDepth" : 25 * mm});
        }
        {
            var Q0;
            Q0=makeQuery(id+"F38.opExtrude","CAP_FACE",FACE,{"disambiguationData":[OSD([sQuery(id+"F37.wireOp",EDGE,"E66"),sQuery(id+"F37.wireOp",EDGE,"E67"),sQuery(id+"F37.wireOp",EDGE,"E68"),sQuery(id+"F37.wireOp",EDGE,"E69"),sQuery(id+"F37.wireOp",EDGE,"E70"),sQuery(id+"F37.wireOp",EDGE,"E71"),sQuery(id+"F37.wireOp",EDGE,"E74")])],"isStart":false});
            var sketch = newSketch(context, id + "F43", { "sketchPlane" : qUnion([Q0])});
            skLineSegment(sketch, "E89", {"start": v(449.5, 39) * mm, "end": v(449.5, 0) * mm});
            skLineSegment(sketch, "E90", {"start": v(449.5, 0) * mm, "end": v(549.5, 0) * mm});
            skLineSegment(sketch, "E91", {"start": v(549.5, 0) * mm, "end": v(549.5, 39) * mm});
            skLineSegment(sketch, "E92", {"start": v(549.5, 39) * mm, "end": v(449.5, 39) * mm});
            skPoint(sketch, "E93", {"position": v(499.5, 0) * mm});
            skCircle(sketch, "E94", {"center": v(499.5, 0) * mm, "radius": 5 * mm});
            skSolve(sketch);
        }
        {
            var Q0;
            Q0 = qSketchRegion(id + "F43", true);
            var Q1;
            {var subQ0=sQuery(id+"F18.wireOp",EDGE,"E37");var subQ1=sQuery(id+"F18.wireOp",EDGE,"E34.MirrorC");var subQ2=sQuery(id+"F18.wireOp",EDGE,"E33");var subQ3=sQuery(id+"F18.wireOp",EDGE,"E32.right");var subQ4=sQuery(id+"F18.wireOp",EDGE,"E32.left");var subQ5=sQuery(id+"F18.wireOp",EDGE,"E32.top");var subQ6=sQuery(id+"F18.wireOp",EDGE,"E32.bottom");var subQ7=sQuery(id+"F16.wireOp",EDGE,"E31");var subQ8=sQuery(id+"F16.wireOp",EDGE,"E30");var subQ9=sQuery(id+"F16.wireOp",EDGE,"E29");var subQ10=sQuery(id+"F16.wireOp",EDGE,"E28");var subQ11=sQuery(id+"F16.wireOp",EDGE,"E27");var subQ12=sQuery(id+"F16.wireOp",EDGE,"E25");var subQ13=sQuery(id+"F16.wireOp",EDGE,"E24");var subQ14=sQuery(id+"F16.wireOp",EDGE,"E23");var subQ15=sQuery(id+"F16.wireOp",EDGE,"E22.MirrorCS");var subQ16=sQuery(id+"F16.wireOp",EDGE,"E19.bottom");Q1=makeQuery(id+"F32.boolean.opBoolean","MERGE",FACE,{"derivedFrom":[makeQuery(id+"F19.boolean.opBoolean","MERGE",FACE,{"derivedFrom":[makeQuery(id+"F17.opExtrude","CAP_FACE",FACE,{"disambiguationData":[OSD([subQ16,subQ15,subQ14,subQ13,subQ12,subQ11,subQ10,subQ9,subQ8,subQ7])],"isStart":false}),makeQuery(id+"F19.opExtrude","CAP_FACE",FACE,{"disambiguationData":[OSD([subQ6,subQ5,subQ4,subQ3,subQ2,subQ1,subQ0])],"isStart":true})]}),makeQuery(id+"F32.opExtrude","CAP_FACE",FACE,{"disambiguationData":[OSD([subQ16,subQ15,subQ14,subQ13,subQ12,subQ11,subQ10,subQ9,subQ8,subQ7,subQ6,subQ5,subQ4,subQ3,subQ2,subQ1,subQ0]),ownerDisambiguation([makeQuery(id+"F32.opExtrude","SWEPT_BODY",BODY,{"disambiguationData":[OSD([sQuery(id+"F31.wireOp",EDGE,"E61"),sQuery(id+"F31.wireOp",EDGE,"E62")])]})])],"isStart":false}),makeQuery(id+"F32.opExtrude","CAP_FACE",FACE,{"disambiguationData":[OSD([subQ16,subQ15,subQ14,subQ13,subQ12,subQ11,subQ10,subQ9,subQ8,subQ7,subQ6,subQ5,subQ4,subQ3,subQ2,subQ1,subQ0]),ownerDisambiguation([makeQuery(id+"F32.opExtrude","SWEPT_BODY",BODY,{"disambiguationData":[OSD([sQuery(id+"F31.wireOp",EDGE,"E63.MirrorC"),sQuery(id+"F31.wireOp",EDGE,"E64.MirrorC")])]})])],"isStart":false})]});}
            extrude(context, id + "F44", {"entities" : qUnion([Q0]), "operationType" : NewBodyOperationType.ADD, "endBound" : BoundingType.UP_TO_SURFACE, "oppositeDirection" : true, "endBoundEntityFace" : qUnion([Q1]), "depth" : 25 * mm});
        }
        {
            var Q0;
            Q0=makeQuery(id+"F38.opExtrude","CAP_FACE",FACE,{"disambiguationData":[OSD([sQuery(id+"F16.wireOp",EDGE,"E19.bottom"),sQuery(id+"F16.wireOp",EDGE,"E22.MirrorCS"),sQuery(id+"F16.wireOp",EDGE,"E23"),sQuery(id+"F16.wireOp",EDGE,"E24"),sQuery(id+"F16.wireOp",EDGE,"E25"),sQuery(id+"F16.wireOp",EDGE,"E27"),sQuery(id+"F16.wireOp",EDGE,"E28"),sQuery(id+"F16.wireOp",EDGE,"E29"),sQuery(id+"F16.wireOp",EDGE,"E30"),sQuery(id+"F16.wireOp",EDGE,"E31"),sQuery(id+"F18.wireOp",EDGE,"E32.bottom"),sQuery(id+"F18.wireOp",EDGE,"E32.top"),sQuery(id+"F18.wireOp",EDGE,"E32.left"),sQuery(id+"F18.wireOp",EDGE,"E32.right"),sQuery(id+"F18.wireOp",EDGE,"E33"),sQuery(id+"F18.wireOp",EDGE,"E34.MirrorC"),sQuery(id+"F18.wireOp",EDGE,"E37")])],"isStart":true});
            var sketch = newSketch(context, id + "F45", { "sketchPlane" : qUnion([Q0])});
            skPoint(sketch, "E95", {"position": v(-529.5, 105) * mm});
            skPoint(sketch, "E96", {"position": v(-529.5, 55) * mm});
            skLineSegment(sketch, "E97", {"start": v(-529.5, 105) * mm, "end": v(-529.5, 55) * mm});
            skLineSegment(sketch, "E98", {"start": v(-529.5, 80) * mm, "end": v(-549.5, 80) * mm});
            skLineSegment(sketch, "E99", {"start": v(-529.5, 105) * mm, "end": v(-549.5, 105) * mm});
            skPoint(sketch, "E100", {"position": v(-549.5, 105) * mm});
            skPoint(sketch, "E101", {"position": v(-549.5, 80) * mm});
            skSolve(sketch);
        }
        {
            var Q0;
            Q0=makeQuery(id+"F44.boolean.opBoolean","MERGE",FACE,{"derivedFrom":[makeQuery(id+"F38.opExtrude","SWEPT_FACE",FACE,{"disambiguationData":[OSD([sQuery(id+"F37.wireOp",EDGE,"E70")])]}),makeQuery(id+"F44.opExtrude","SWEPT_FACE",FACE,{"disambiguationData":[OSD([sQuery(id+"F43.wireOp",EDGE,"E91")])]})]});
            var sketch = newSketch(context, id + "F46", { "sketchPlane" : qUnion([Q0])});
            skLineSegment(sketch, "E102.bottom", {"start": v(15, 75) * mm, "end": v(25, 75) * mm});
            skLineSegment(sketch, "E102.top", {"start": v(15, 85) * mm, "end": v(25, 85) * mm});
            skLineSegment(sketch, "E102.left", {"start": v(15, 75) * mm, "end": v(15, 85) * mm});
            skLineSegment(sketch, "E102.right", {"start": v(25, 75) * mm, "end": v(25, 85) * mm});
            skPoint(sketch, "E103", {"position": v(25, 80) * mm});
            skCircle(sketch, "E104", {"center": v(25, 80) * mm, "radius": 5 * mm});
            skPoint(sketch, "E105", {"position": v(15, 80) * mm});
            skPoint(sketch, "E106.MirrorP", {"position": v(15, 129.82) * mm});
            skLineSegment(sketch, "E107", {"start": v(15, 105) * mm, "end": v(27.48, 105) * mm, "construction": true});
            skLineSegment(sketch, "E108.MirrorCS", {"start": v(15, 125) * mm, "end": v(25, 125) * mm});
            skLineSegment(sketch, "E109.MirrorCS", {"start": v(15, 135) * mm, "end": v(25, 135) * mm});
            skCircle(sketch, "E110.MirrorC", {"center": v(25, 130) * mm, "radius": 5 * mm});
            skLineSegment(sketch, "E111.MirrorCS", {"start": v(15, 135) * mm, "end": v(15, 125) * mm});
            skPoint(sketch, "E112.MirrorP", {"position": v(15, 130) * mm});
            skCircle(sketch, "E113", {"center": v(25, 80) * mm, "radius": 2.5 * mm});
            skCircle(sketch, "E114.MirrorC", {"center": v(25, 130) * mm, "radius": 2.5 * mm});
            skSolve(sketch);
        }
        {
            var Q0;
            Q0 = qSketchRegion(id + "F46", true);
            extrude(context, id + "F47", {"entities" : qUnion([Q0]), "operationType" : NewBodyOperationType.ADD, "oppositeDirection" : true, "depth" : 10 * mm});
        }
    });
